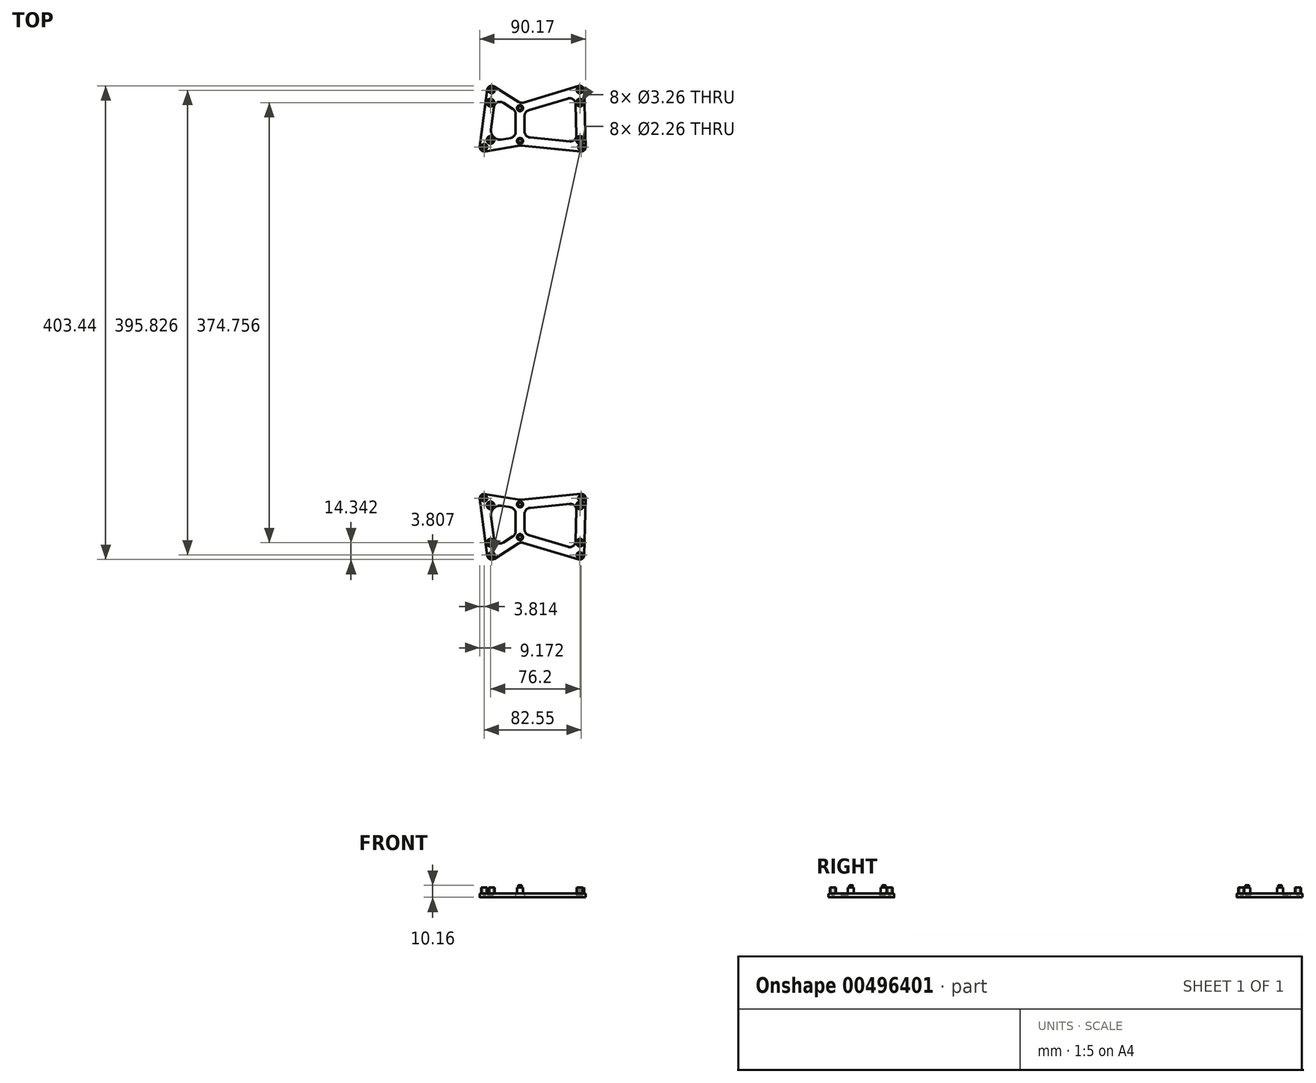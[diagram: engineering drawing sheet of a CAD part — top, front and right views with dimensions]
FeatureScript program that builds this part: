
annotation { "Feature Type Name" : "Feature", "Feature Type Description" : "" }
export const myFeature = defineFeature(function(context is Context, id is Id, definition is map)
    precondition{}
    {
        {
            var Q0;
            Q0=qCreatedBy(makeId("Top.planeOp"),FACE);
            var sketch = newSketch(context, id + "F0", { "sketchPlane" : qUnion([Q0])});
            skArc(sketch, "E0", {"start": v(-29.84, 201.13) * mm, "mid": v(-33.5, 201.36) * mm, "end": v(-35.65, 198.4) * mm});
            skArc(sketch, "E1", {"start": v(-42, 150.15) * mm, "mid": v(-40.87, 146.91) * mm, "end": v(-37.6, 145.9) * mm});
            skArc(sketch, "E2", {"start": v(46.86, 198.01) * mm, "mid": v(45.29, 201) * mm, "end": v(41.96, 201.56) * mm});
            skArc(sketch, "E3", {"start": v(43.95, 145.86) * mm, "mid": v(46.92, 146.86) * mm, "end": v(48.13, 149.75) * mm});
            skLineSegment(sketch, "E4", {"start": v(-35.65, 198.4) * mm, "end": v(-42, 150.15) * mm});
            skLineSegment(sketch, "E5", {"start": v(-29.84, 201.13) * mm, "end": v(-9.13, 188.06) * mm});
            skLineSegment(sketch, "E6", {"start": v(-37.6, 145.9) * mm, "end": v(-8.24, 150.79) * mm});
            skLineSegment(sketch, "E7", {"start": v(-4.96, 187.49) * mm, "end": v(41.96, 201.56) * mm});
            skLineSegment(sketch, "E8", {"start": v(-6.91, 150.83) * mm, "end": v(43.95, 145.86) * mm});
            skLineSegment(sketch, "E9", {"start": v(46.86, 198.01) * mm, "end": v(48.13, 149.75) * mm});
            skLineSegment(sketch, "E10", {"start": v(33.01, 190.92) * mm, "end": v(-0.32, 180.92) * mm});
            skLineSegment(sketch, "E11", {"start": v(-22.16, 187.27) * mm, "end": v(-13.92, 182.07) * mm});
            skLineSegment(sketch, "E12", {"start": v(-23.63, 155.95) * mm, "end": v(-15.8, 157.25) * mm});
            skLineSegment(sketch, "E13", {"start": v(0.65, 157.74) * mm, "end": v(34.68, 154.42) * mm});
            skLineSegment(sketch, "E14", {"start": v(40.25, 159.61) * mm, "end": v(39.55, 186.2) * mm});
            skLineSegment(sketch, "E15", {"start": v(-29.91, 183.64) * mm, "end": v(-32.43, 164.46) * mm});
            skLineSegment(sketch, "E16", {"start": v(-11.56, 177.77) * mm, "end": v(-11.56, 162.26) * mm});
            skLineSegment(sketch, "E17", {"start": v(-3.94, 176.06) * mm, "end": v(-3.94, 162.8) * mm});
            skArc(sketch, "E18.filletArc", {"start": v(-22.16, 187.27) * mm, "mid": v(-27.03, 187.58) * mm, "end": v(-29.91, 183.64) * mm});
            skArc(sketch, "E19.filletArc", {"start": v(-32.43, 164.46) * mm, "mid": v(-30.17, 157.99) * mm, "end": v(-23.63, 155.95) * mm});
            skArc(sketch, "E20.filletArc", {"start": v(-15.8, 157.25) * mm, "mid": v(-12.76, 158.98) * mm, "end": v(-11.56, 162.26) * mm});
            skArc(sketch, "E21.filletArc", {"start": v(-11.56, 177.77) * mm, "mid": v(-12.19, 180.23) * mm, "end": v(-13.92, 182.07) * mm});
            skArc(sketch, "E22.filletArc", {"start": v(-9.13, 188.06) * mm, "mid": v(-7.11, 187.32) * mm, "end": v(-4.96, 187.49) * mm});
            skArc(sketch, "E23.filletArc", {"start": v(-0.32, 180.92) * mm, "mid": v(-2.93, 179.1) * mm, "end": v(-3.94, 176.06) * mm});
            skArc(sketch, "E24.filletArc", {"start": v(-3.94, 162.8) * mm, "mid": v(-2.62, 159.38) * mm, "end": v(0.65, 157.74) * mm});
            skArc(sketch, "E25.filletArc", {"start": v(34.68, 154.42) * mm, "mid": v(38.64, 155.76) * mm, "end": v(40.25, 159.61) * mm});
            skArc(sketch, "E26.filletArc", {"start": v(39.55, 186.2) * mm, "mid": v(37.45, 190.17) * mm, "end": v(33.01, 190.92) * mm});
            skPoint(sketch, "E27", {"position": v(-7.75, 154.73) * mm});
            skPoint(sketch, "E28", {"position": v(-7.75, 182.67) * mm});
            skCircle(sketch, "E29", {"center": v(-31.88, 197.91) * mm, "radius": 2.54 * mm});
            skCircle(sketch, "E30", {"center": v(-38.23, 149.65) * mm, "radius": 2.54 * mm});
            skCircle(sketch, "E31", {"center": v(-7.75, 154.73) * mm, "radius": 2.54 * mm});
            skCircle(sketch, "E32", {"center": v(-7.75, 182.67) * mm, "radius": 2.54 * mm});
            skCircle(sketch, "E33", {"center": v(43.05, 197.91) * mm, "radius": 2.54 * mm});
            skCircle(sketch, "E34", {"center": v(44.32, 149.65) * mm, "radius": 2.54 * mm});
            skPoint(sketch, "E35.newPointA", {"position": v(-7.12, 150.97) * mm});
            skPoint(sketch, "E35.newPointB", {"position": v(-8.37, 150.97) * mm});
            skArc(sketch, "E35.filletArc", {"start": v(-6.91, 150.83) * mm, "mid": v(-7.58, 150.85) * mm, "end": v(-8.24, 150.79) * mm});
            skSolve(sketch);
        }
        {
            var Q0;
            Q0 = qSketchRegion(id + "F0", true);
            extrude(context, id + "F1", {"entities" : qUnion([Q0]), "depth" : 3.17 * mm, "offsetDistance" : 25.4 * mm});
        }
        {
            var Q0;
            Q0=makeQuery(id+"F1.opExtrude","CAP_FACE",FACE,{"disambiguationData":[OSD([sQuery(id+"F0.wireOp",EDGE,"E0"),sQuery(id+"F0.wireOp",EDGE,"E1"),sQuery(id+"F0.wireOp",EDGE,"c3ae1f5f-e9c8-4c9f-a5ed-62b5cc151e64"),sQuery(id+"F0.wireOp",EDGE,"E2"),sQuery(id+"F0.wireOp",EDGE,"E3"),sQuery(id+"F0.wireOp",EDGE,"E4"),sQuery(id+"F0.wireOp",EDGE,"E5"),sQuery(id+"F0.wireOp",EDGE,"E6"),sQuery(id+"F0.wireOp",EDGE,"E7"),sQuery(id+"F0.wireOp",EDGE,"E8"),sQuery(id+"F0.wireOp",EDGE,"E9"),sQuery(id+"F0.wireOp",EDGE,"E10"),sQuery(id+"F0.wireOp",EDGE,"E11"),sQuery(id+"F0.wireOp",EDGE,"E12"),sQuery(id+"F0.wireOp",EDGE,"E13"),sQuery(id+"F0.wireOp",EDGE,"E14"),sQuery(id+"F0.wireOp",EDGE,"E15"),sQuery(id+"F0.wireOp",EDGE,"E16"),sQuery(id+"F0.wireOp",EDGE,"E17"),sQuery(id+"F0.wireOp",EDGE,"E18.filletArc"),sQuery(id+"F0.wireOp",EDGE,"E19.filletArc"),sQuery(id+"F0.wireOp",EDGE,"E20.filletArc"),sQuery(id+"F0.wireOp",EDGE,"E21.filletArc"),sQuery(id+"F0.wireOp",EDGE,"E22.filletArc"),sQuery(id+"F0.wireOp",EDGE,"E23.filletArc"),sQuery(id+"F0.wireOp",EDGE,"E24.filletArc"),sQuery(id+"F0.wireOp",EDGE,"E25.filletArc"),sQuery(id+"F0.wireOp",EDGE,"E26.filletArc"),sQuery(id+"F0.wireOp",EDGE,"E29"),sQuery(id+"F0.wireOp",EDGE,"E30"),sQuery(id+"F0.wireOp",EDGE,"E31"),sQuery(id+"F0.wireOp",EDGE,"E32"),sQuery(id+"F0.wireOp",EDGE,"E33"),sQuery(id+"F0.wireOp",EDGE,"E34")])],"isStart":false});
            var sketch = newSketch(context, id + "F2", { "sketchPlane" : qUnion([Q0])});
            skCircle(sketch, "E36", {"center": v(-31.88, 197.91) * mm, "radius": 2.54 * mm});
            skCircle(sketch, "E37", {"center": v(-38.23, 149.65) * mm, "radius": 2.54 * mm});
            skCircle(sketch, "E38", {"center": v(-7.75, 182.67) * mm, "radius": 2.54 * mm});
            skCircle(sketch, "E39", {"center": v(-7.75, 154.73) * mm, "radius": 2.54 * mm});
            skCircle(sketch, "E40", {"center": v(43.05, 197.91) * mm, "radius": 2.54 * mm});
            skCircle(sketch, "E41", {"center": v(44.32, 149.65) * mm, "radius": 2.54 * mm});
            skSolve(sketch);
        }
        {
            var Q0;
            Q0 = qSketchRegion(id + "F2", true);
            extrude(context, id + "F3", {"entities" : qUnion([Q0]), "operationType" : NewBodyOperationType.ADD, "depth" : 5.08 * mm, "offsetDistance" : 25.4 * mm, "hasSecondDirection" : true, "secondDirectionOppositeDirection" : true, "secondDirectionDepth" : 3.17 * mm});
        }
        {
            var Q0;
            Q0=makeQuery(id+"F1.opExtrude","CAP_FACE",FACE,{"disambiguationData":[OSD([sQuery(id+"F0.wireOp",EDGE,"E0"),sQuery(id+"F0.wireOp",EDGE,"E1"),sQuery(id+"F0.wireOp",EDGE,"c3ae1f5f-e9c8-4c9f-a5ed-62b5cc151e64"),sQuery(id+"F0.wireOp",EDGE,"E2"),sQuery(id+"F0.wireOp",EDGE,"E3"),sQuery(id+"F0.wireOp",EDGE,"E4"),sQuery(id+"F0.wireOp",EDGE,"E5"),sQuery(id+"F0.wireOp",EDGE,"E6"),sQuery(id+"F0.wireOp",EDGE,"E7"),sQuery(id+"F0.wireOp",EDGE,"E8"),sQuery(id+"F0.wireOp",EDGE,"E9"),sQuery(id+"F0.wireOp",EDGE,"E10"),sQuery(id+"F0.wireOp",EDGE,"E11"),sQuery(id+"F0.wireOp",EDGE,"E12"),sQuery(id+"F0.wireOp",EDGE,"E13"),sQuery(id+"F0.wireOp",EDGE,"E14"),sQuery(id+"F0.wireOp",EDGE,"E15"),sQuery(id+"F0.wireOp",EDGE,"E16"),sQuery(id+"F0.wireOp",EDGE,"E17"),sQuery(id+"F0.wireOp",EDGE,"E18.filletArc"),sQuery(id+"F0.wireOp",EDGE,"E19.filletArc"),sQuery(id+"F0.wireOp",EDGE,"E20.filletArc"),sQuery(id+"F0.wireOp",EDGE,"E21.filletArc"),sQuery(id+"F0.wireOp",EDGE,"E22.filletArc"),sQuery(id+"F0.wireOp",EDGE,"E23.filletArc"),sQuery(id+"F0.wireOp",EDGE,"E24.filletArc"),sQuery(id+"F0.wireOp",EDGE,"E25.filletArc"),sQuery(id+"F0.wireOp",EDGE,"E26.filletArc"),sQuery(id+"F0.wireOp",EDGE,"E29"),sQuery(id+"F0.wireOp",EDGE,"E30"),sQuery(id+"F0.wireOp",EDGE,"E31"),sQuery(id+"F0.wireOp",EDGE,"E32"),sQuery(id+"F0.wireOp",EDGE,"E33"),sQuery(id+"F0.wireOp",EDGE,"E34")])],"isStart":false});
            var sketch = newSketch(context, id + "F4", { "sketchPlane" : qUnion([Q0])});
            skPoint(sketch, "E42", {"position": v(-32.87, 187.38) * mm});
            skPoint(sketch, "E43", {"position": v(43.33, 187.38) * mm});
            skPoint(sketch, "E44", {"position": v(43.33, 155.63) * mm});
            skPoint(sketch, "E45", {"position": v(-32.87, 155.63) * mm});
            skSolve(sketch);
        }
        {
            var Q0;
            Q0=sQuery(id+"F4.wireOp",VERTEX,"E45");
            var Q1;
            Q1=sQuery(id+"F4.wireOp",VERTEX,"E42");
            var Q2;
            Q2=sQuery(id+"F4.wireOp",VERTEX,"E43");
            var Q3;
            Q3=sQuery(id+"F4.wireOp",VERTEX,"E44");
            var Q4;
            Q4=makeQuery(id+"F1.opExtrude","SWEPT_BODY",BODY,{"disambiguationData":[OSD([sQuery(id+"F0.wireOp",EDGE,"E0"),sQuery(id+"F0.wireOp",EDGE,"E1"),sQuery(id+"F0.wireOp",EDGE,"c3ae1f5f-e9c8-4c9f-a5ed-62b5cc151e64"),sQuery(id+"F0.wireOp",EDGE,"E2"),sQuery(id+"F0.wireOp",EDGE,"E3"),sQuery(id+"F0.wireOp",EDGE,"E4"),sQuery(id+"F0.wireOp",EDGE,"E5"),sQuery(id+"F0.wireOp",EDGE,"E6"),sQuery(id+"F0.wireOp",EDGE,"E7"),sQuery(id+"F0.wireOp",EDGE,"E8"),sQuery(id+"F0.wireOp",EDGE,"E9"),sQuery(id+"F0.wireOp",EDGE,"E10"),sQuery(id+"F0.wireOp",EDGE,"E11"),sQuery(id+"F0.wireOp",EDGE,"E12"),sQuery(id+"F0.wireOp",EDGE,"E13"),sQuery(id+"F0.wireOp",EDGE,"E14"),sQuery(id+"F0.wireOp",EDGE,"E15"),sQuery(id+"F0.wireOp",EDGE,"E16"),sQuery(id+"F0.wireOp",EDGE,"E17"),sQuery(id+"F0.wireOp",EDGE,"E18.filletArc"),sQuery(id+"F0.wireOp",EDGE,"E19.filletArc"),sQuery(id+"F0.wireOp",EDGE,"E20.filletArc"),sQuery(id+"F0.wireOp",EDGE,"E21.filletArc"),sQuery(id+"F0.wireOp",EDGE,"E22.filletArc"),sQuery(id+"F0.wireOp",EDGE,"E23.filletArc"),sQuery(id+"F0.wireOp",EDGE,"E24.filletArc"),sQuery(id+"F0.wireOp",EDGE,"E25.filletArc"),sQuery(id+"F0.wireOp",EDGE,"E26.filletArc"),sQuery(id+"F0.wireOp",EDGE,"E29"),sQuery(id+"F0.wireOp",EDGE,"E30"),sQuery(id+"F0.wireOp",EDGE,"E31"),sQuery(id+"F0.wireOp",EDGE,"E32"),sQuery(id+"F0.wireOp",EDGE,"E33"),sQuery(id+"F0.wireOp",EDGE,"E34")])]});
            hole(context, id + "F5", {"style" : HoleStyle.C_SINK, "endStyle" : HoleEndStyle.THROUGH, "standardTappedOrClearance" : lookupTablePath({ "standard" : "ANSI", "fit" : "Normal (ASME)", "size" : "#4", "type" : "Clearance" }), "standardBlindInLast" : lookupTablePath({ "fit" : "Free", "standard" : "ANSI", "size" : "#4", "type" : "Clearance" }), "holeDiameter" : 3.26 * mm, "cSinkDiameter" : 6.48 * mm, "cSinkAngle" : 82 * degree, "tappedDepth" : 12.7 * mm, "tapClearance" : 3, "locations" : qUnion([Q0, Q1, Q2, Q3]), "scope" : qUnion([Q4])});
        }
        {
            var Q0;
            Q0=makeQuery(id+"F3.opExtrude","CAP_FACE",FACE,{"disambiguationData":[OSD([sQuery(id+"F2.wireOp",EDGE,"E36")])],"isStart":false});
            var sketch = newSketch(context, id + "F6", { "sketchPlane" : qUnion([Q0])});
            skPoint(sketch, "E46", {"position": v(-31.88, 197.91) * mm});
            skPoint(sketch, "E47", {"position": v(-38.23, 149.65) * mm});
            skPoint(sketch, "E48", {"position": v(44.32, 149.65) * mm});
            skPoint(sketch, "E49", {"position": v(43.05, 197.91) * mm});
            skSolve(sketch);
        }
        {
            var Q0;
            Q0=sQuery(id+"F6.wireOp",VERTEX,"E46");
            var Q1;
            Q1=sQuery(id+"F6.wireOp",VERTEX,"E47");
            var Q2;
            Q2=sQuery(id+"F6.wireOp",VERTEX,"E49");
            var Q3;
            Q3=sQuery(id+"F6.wireOp",VERTEX,"E48");
            var Q4;
            Q4=makeQuery(id+"F1.opExtrude","SWEPT_BODY",BODY,{"disambiguationData":[OSD([sQuery(id+"F0.wireOp",EDGE,"E0"),sQuery(id+"F0.wireOp",EDGE,"E1"),sQuery(id+"F0.wireOp",EDGE,"c3ae1f5f-e9c8-4c9f-a5ed-62b5cc151e64"),sQuery(id+"F0.wireOp",EDGE,"E2"),sQuery(id+"F0.wireOp",EDGE,"E3"),sQuery(id+"F0.wireOp",EDGE,"E4"),sQuery(id+"F0.wireOp",EDGE,"E5"),sQuery(id+"F0.wireOp",EDGE,"E6"),sQuery(id+"F0.wireOp",EDGE,"E7"),sQuery(id+"F0.wireOp",EDGE,"E8"),sQuery(id+"F0.wireOp",EDGE,"E9"),sQuery(id+"F0.wireOp",EDGE,"E10"),sQuery(id+"F0.wireOp",EDGE,"E11"),sQuery(id+"F0.wireOp",EDGE,"E12"),sQuery(id+"F0.wireOp",EDGE,"E13"),sQuery(id+"F0.wireOp",EDGE,"E14"),sQuery(id+"F0.wireOp",EDGE,"E15"),sQuery(id+"F0.wireOp",EDGE,"E16"),sQuery(id+"F0.wireOp",EDGE,"E17"),sQuery(id+"F0.wireOp",EDGE,"E18.filletArc"),sQuery(id+"F0.wireOp",EDGE,"E19.filletArc"),sQuery(id+"F0.wireOp",EDGE,"E20.filletArc"),sQuery(id+"F0.wireOp",EDGE,"E21.filletArc"),sQuery(id+"F0.wireOp",EDGE,"E22.filletArc"),sQuery(id+"F0.wireOp",EDGE,"E23.filletArc"),sQuery(id+"F0.wireOp",EDGE,"E24.filletArc"),sQuery(id+"F0.wireOp",EDGE,"E25.filletArc"),sQuery(id+"F0.wireOp",EDGE,"E26.filletArc"),sQuery(id+"F0.wireOp",EDGE,"E29"),sQuery(id+"F0.wireOp",EDGE,"E30"),sQuery(id+"F0.wireOp",EDGE,"E31"),sQuery(id+"F0.wireOp",EDGE,"E32"),sQuery(id+"F0.wireOp",EDGE,"E33"),sQuery(id+"F0.wireOp",EDGE,"E34")])]});
            hole(context, id + "F7", {"style" : HoleStyle.SIMPLE, "endStyle" : HoleEndStyle.BLIND, "standardTappedOrClearance" : lookupTablePath({ "standard" : "ANSI", "engagement" : "75%", "pitch" : "40 tpi", "size" : "#4", "type" : "Tapped" }), "standardBlindInLast" : lookupTablePath({ "standard" : "ANSI", "engagement" : "75%", "pitch" : "40 tpi", "size" : "#4", "type" : "Tapped" }), "holeDiameter" : 2.26 * mm, "showTappedDepth" : true, "holeDepth" : 6.35 * mm, "tappedDepth" : 4.44 * mm, "tapClearance" : 3, "locations" : qUnion([Q0, Q1, Q2, Q3]), "scope" : qUnion([Q4]), "majorDiameter" : 2.84 * mm});
        }
        {
            var Q0;
            Q0=makeQuery(id+"F3.opExtrude","CAP_FACE",FACE,{"disambiguationData":[OSD([sQuery(id+"F2.wireOp",EDGE,"E38")])],"isStart":false});
            var sketch = newSketch(context, id + "F8", { "sketchPlane" : qUnion([Q0])});
            skPoint(sketch, "E50", {"position": v(-7.75, 182.67) * mm});
            skPoint(sketch, "E51", {"position": v(-7.75, 154.73) * mm});
            skCircle(sketch, "E52", {"center": v(-7.75, 182.67) * mm, "radius": 1.5 * mm});
            skCircle(sketch, "E53", {"center": v(-7.75, 154.73) * mm, "radius": 1.5 * mm});
            skSolve(sketch);
        }
        {
            var Q0;
            Q0 = qSketchRegion(id + "F8", true);
            extrude(context, id + "F9", {"entities" : qUnion([Q0]), "operationType" : NewBodyOperationType.ADD, "depth" : 1.9 * mm, "offsetDistance" : 25.4 * mm});
        }
        {
            var Q0;
            Q0=makeQuery(id+"F1.opExtrude","CAP_EDGE",EDGE,{"disambiguationData":[OSD([sQuery(id+"F0.wireOp",EDGE,"E6")])],"isStart":false});
            var Q1;
            Q1=makeQuery(id+"F1.opExtrude","CAP_EDGE",EDGE,{"disambiguationData":[OSD([sQuery(id+"F0.wireOp",EDGE,"E18.filletArc")])],"isStart":false});
            var Q2;
            Q2=makeQuery(id+"F1.opExtrude","CAP_EDGE",EDGE,{"disambiguationData":[OSD([sQuery(id+"F0.wireOp",EDGE,"E10")])],"isStart":false});
            var Q3;
            Q3=makeQuery(id+"F1.opExtrude","CAP_EDGE",EDGE,{"disambiguationData":[OSD([sQuery(id+"F0.wireOp",EDGE,"E30")])],"isStart":false});
            var Q4;
            Q4=makeQuery(id+"F1.opExtrude","CAP_EDGE",EDGE,{"disambiguationData":[OSD([sQuery(id+"F0.wireOp",EDGE,"E31")])],"isStart":false});
            var Q5;
            Q5=makeQuery(id+"F1.opExtrude","CAP_EDGE",EDGE,{"disambiguationData":[OSD([sQuery(id+"F0.wireOp",EDGE,"E32")])],"isStart":false});
            var Q6;
            Q6=makeQuery(id+"F1.opExtrude","CAP_EDGE",EDGE,{"disambiguationData":[OSD([sQuery(id+"F0.wireOp",EDGE,"E29")])],"isStart":false});
            var Q7;
            Q7=makeQuery(id+"F1.opExtrude","CAP_EDGE",EDGE,{"disambiguationData":[OSD([sQuery(id+"F0.wireOp",EDGE,"E33")])],"isStart":false});
            var Q8;
            Q8=makeQuery(id+"F1.opExtrude","CAP_EDGE",EDGE,{"disambiguationData":[OSD([sQuery(id+"F0.wireOp",EDGE,"E34")])],"isStart":false});
            fillet(context, id + "F10", {"entities" : qUnion([Q0, Q1, Q2, Q3, Q4, Q5, Q6, Q7, Q8]), "radius" : 0.64 * mm, "tangentPropagation" : true, "allowEdgeOverflow" : false});
        }
        {
            var Q0;
            Q0=makeQuery(id+"F1.opExtrude","SWEPT_BODY",BODY,{"disambiguationData":[OSD([sQuery(id+"F0.wireOp",EDGE,"E0"),sQuery(id+"F0.wireOp",EDGE,"E1"),sQuery(id+"F0.wireOp",EDGE,"E2"),sQuery(id+"F0.wireOp",EDGE,"E3"),sQuery(id+"F0.wireOp",EDGE,"E4"),sQuery(id+"F0.wireOp",EDGE,"E5"),sQuery(id+"F0.wireOp",EDGE,"E6"),sQuery(id+"F0.wireOp",EDGE,"E7"),sQuery(id+"F0.wireOp",EDGE,"E8"),sQuery(id+"F0.wireOp",EDGE,"E9"),sQuery(id+"F0.wireOp",EDGE,"E10"),sQuery(id+"F0.wireOp",EDGE,"E11"),sQuery(id+"F0.wireOp",EDGE,"E12"),sQuery(id+"F0.wireOp",EDGE,"E13"),sQuery(id+"F0.wireOp",EDGE,"E14"),sQuery(id+"F0.wireOp",EDGE,"E15"),sQuery(id+"F0.wireOp",EDGE,"E16"),sQuery(id+"F0.wireOp",EDGE,"E17"),sQuery(id+"F0.wireOp",EDGE,"E18.filletArc"),sQuery(id+"F0.wireOp",EDGE,"E19.filletArc"),sQuery(id+"F0.wireOp",EDGE,"E20.filletArc"),sQuery(id+"F0.wireOp",EDGE,"E21.filletArc"),sQuery(id+"F0.wireOp",EDGE,"E22.filletArc"),sQuery(id+"F0.wireOp",EDGE,"E23.filletArc"),sQuery(id+"F0.wireOp",EDGE,"E24.filletArc"),sQuery(id+"F0.wireOp",EDGE,"E25.filletArc"),sQuery(id+"F0.wireOp",EDGE,"E26.filletArc"),sQuery(id+"F0.wireOp",EDGE,"E29"),sQuery(id+"F0.wireOp",EDGE,"E30"),sQuery(id+"F0.wireOp",EDGE,"E31"),sQuery(id+"F0.wireOp",EDGE,"E32"),sQuery(id+"F0.wireOp",EDGE,"E33"),sQuery(id+"F0.wireOp",EDGE,"E34"),sQuery(id+"F0.wireOp",EDGE,"E35.filletArc")])]});
            var Q1;
            Q1=qCreatedBy(makeId("Front.planeOp"),FACE);
            mirror(context, id + "F11", {"entities" : qUnion([Q0]), "mirrorPlane" : qUnion([Q1])});
        }
    });
